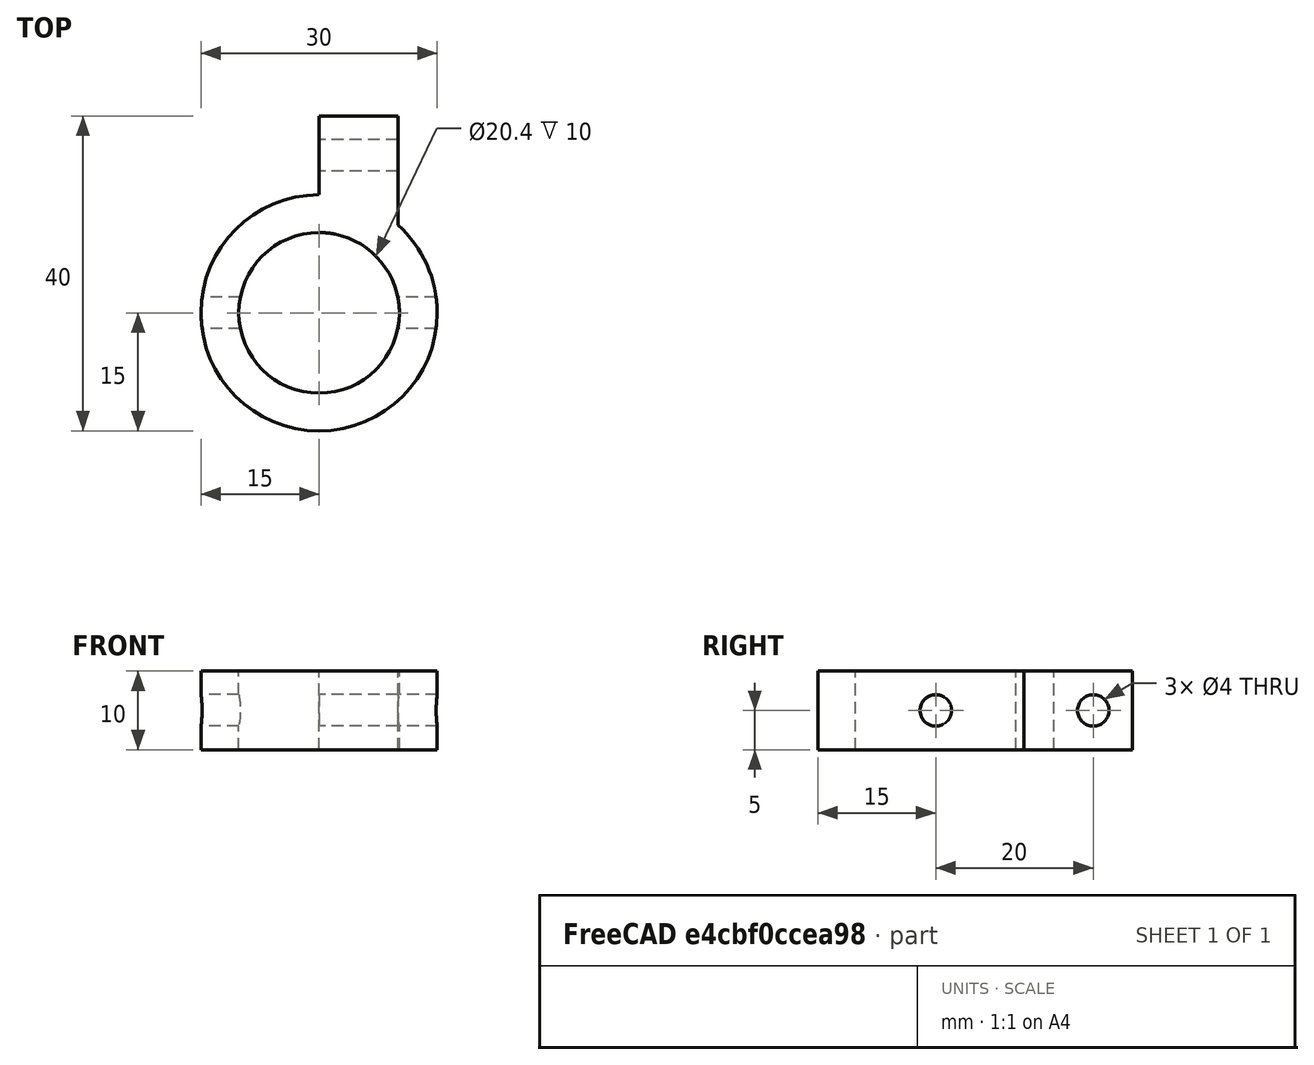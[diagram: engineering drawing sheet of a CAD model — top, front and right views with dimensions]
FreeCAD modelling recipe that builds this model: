
FCSTD DOCUMENT  (FreeCAD 0.18R16110 (Git))
Label: BaseAttachment
License: All rights reserved
LicenseURL: http://en.wikipedia.org/wiki/All_rights_reserved
objects: Part::Cylinder×4, Part::MultiFuse×2, Part::Box×1, Part::Cut×1
note: 8 computed .brp shape members not serialized (recipe doc carries the construction recipe); baked Part::Feature solids carry a one-line shape summary decoded from their .brp

FEATURE [Part::Cylinder] Cylinder
  Angle = 360
  AttacherType = Attacher::AttachEngine3D
  Height = 10
  Placement = pos=(0,0,-5) rot=(0,0,1;0rad)
  Radius = 15
FEATURE [Part::Cylinder] Cylinder001
  Angle = 360
  AttacherType = Attacher::AttachEngine3D
  Height = 10
  Placement = pos=(0,0,-5) rot=(0,0,1;0rad)
  Radius = 10.2
FEATURE [Part::Box] Box  label="Cube"
  AttacherType = Attacher::AttachEngine3D
  Height = 10
  Length = 10
  Placement = pos=(0,10,-5) rot=(0,0,1;0rad)
  Width = 15
FEATURE [Part::Cylinder] Cylinder003
  Angle = 360
  AttacherType = Attacher::AttachEngine3D
  Height = 10
  Placement = pos=(10,20,1e-15) rot=(0,-1,0;1.5708rad)
  Radius = 2
FEATURE [Part::MultiFuse] Fusion001  label="Positive Fusion"
  Shapes = -> [Cylinder,Box]
FEATURE [Part::Cylinder] Cylinder004
  Angle = 360
  AttacherType = Attacher::AttachEngine3D
  Height = 30
  Placement = pos=(15,0,0) rot=(0,-1,0;1.5708rad)
  Radius = 2
FEATURE [Part::MultiFuse] Fusion  label="Negative Fusion"
  Shapes = -> [Cylinder001,Cylinder003,Cylinder004]
FEATURE [Part::Cut] Cut
  Base = -> Fusion001
  Tool = -> Fusion
